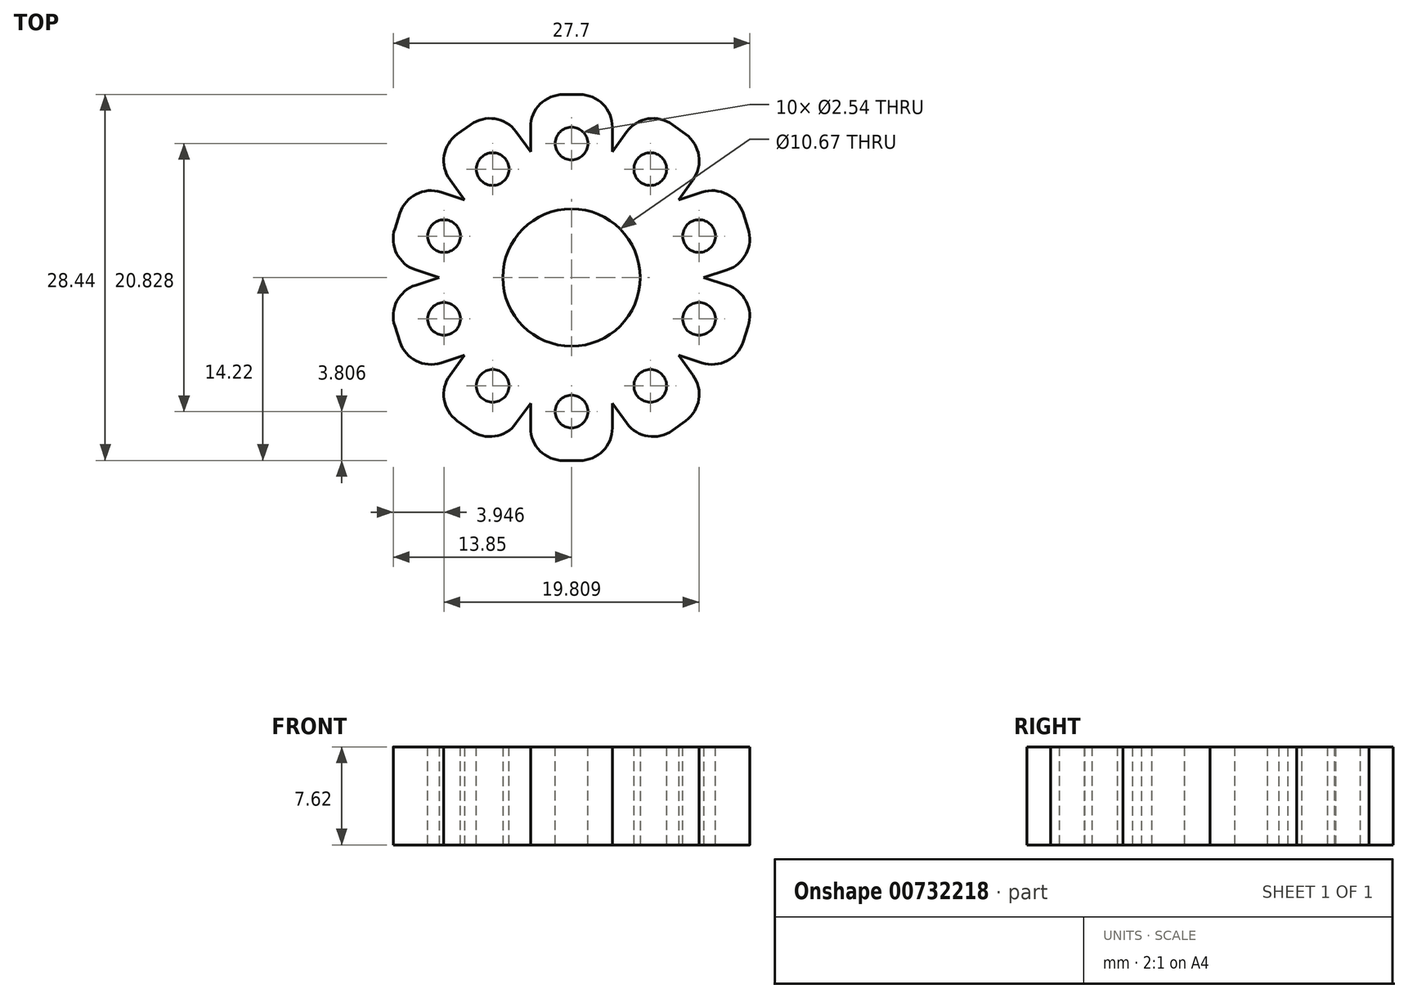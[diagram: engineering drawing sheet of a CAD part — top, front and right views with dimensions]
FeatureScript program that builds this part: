
annotation { "Feature Type Name" : "Feature", "Feature Type Description" : "" }
export const myFeature = defineFeature(function(context is Context, id is Id, definition is map)
    precondition{}
    {
        {
            var Q0;
            Q0=qCreatedBy(makeId("Top.planeOp"),FACE);
            var sketch = newSketch(context, id + "F0", { "sketchPlane" : qUnion([Q0])});
            skCircle(sketch, "E0", {"center": v(0, 0) * mm, "radius": 5.33 * mm});
            skCircle(sketch, "E1", {"center": v(0, 0) * mm, "radius": 7.62 * mm});
            skSolve(sketch);
        }
        {
            var Q0;
            Q0=makeQuery(id+"F0.imprint","IMPRINT",FACE,{"disambiguationData":[TD([[makeQuery(id+"F0.imprint","IMPRINT",EDGE,{"derivedFrom":sQuery(id+"F0.wireOp",EDGE,"E0")}),-1.0]])]});
            extrude(context, id + "F1", {"entities" : qUnion([Q0]), "depth" : 7.62 * mm, "offsetDistance" : 25.4 * mm});
        }
        {
            var Q0;
            Q0=makeQuery(id+"F1.opExtrude","CAP_FACE",FACE,{"disambiguationData":[OSD([sQuery(id+"F0.wireOp",EDGE,"E0"),sQuery(id+"F0.wireOp",EDGE,"E1")])],"isStart":false});
            var sketch = newSketch(context, id + "F2", { "sketchPlane" : qUnion([Q0])});
            skLineSegment(sketch, "E2", {"start": v(3.18, 5.33) * mm, "end": v(-3.18, 5.33) * mm});
            skLineSegment(sketch, "E3", {"start": v(-3.17, 5.33) * mm, "end": v(-3.18, 14.22) * mm});
            skLineSegment(sketch, "E4", {"start": v(-3.18, 14.22) * mm, "end": v(3.17, 14.22) * mm});
            skLineSegment(sketch, "E5", {"start": v(3.17, 14.22) * mm, "end": v(3.18, 5.33) * mm});
            skCircle(sketch, "E6", {"center": v(0, 10.41) * mm, "radius": 1.27 * mm});
            skSolve(sketch);
        }
        {
            var Q0;
            {var subQ1=sQuery(id+"F2.wireOp",EDGE,"E4");Q0=makeQuery(id+"F2.imprint","IMPRINT",FACE,{"disambiguationData":[TD([[makeQuery(id+"F2.imprint","IMPRINT",EDGE,{"derivedFrom":subQ1}),-1.0]])]});}
            extrude(context, id + "F3", {"entities" : qUnion([Q0]), "operationType" : NewBodyOperationType.ADD, "oppositeDirection" : true, "depth" : 7.62 * mm, "offsetDistance" : 25.4 * mm});
        }
        {
            var Q0;
            Q0=makeQuery(id+"F3.opExtrude","SWEPT_EDGE",EDGE,{"disambiguationData":[OSD([sQuery(id+"F2.wireOp",EDGE,"E4"),sQuery(id+"F2.wireOp",EDGE,"E5")])]});
            var Q1;
            Q1=makeQuery(id+"F3.opExtrude","SWEPT_EDGE",EDGE,{"disambiguationData":[OSD([sQuery(id+"F2.wireOp",EDGE,"E3"),sQuery(id+"F2.wireOp",EDGE,"E4")])]});
            fillet(context, id + "F4", {"entities" : qUnion([Q0, Q1]), "radius" : 2.54 * mm, "tangentPropagation" : true, "allowEdgeOverflow" : false});
        }
        {
            var Q0;
            Q0=makeQuery(id+"F1.opExtrude","SWEPT_BODY",BODY,{"disambiguationData":[OSD([sQuery(id+"F0.wireOp",EDGE,"E0"),sQuery(id+"F0.wireOp",EDGE,"E1")])]});
            var Q1;
            Q1=makeQuery(id+"F1.opExtrude","CAP_EDGE",EDGE,{"disambiguationData":[OSD([sQuery(id+"F0.wireOp",EDGE,"E0")])],"isStart":true});
            circularPattern(context, id + "F5", {"operationType" : NewBodyOperationType.ADD, "entities" : qUnion([Q0]), "axis" : qUnion([Q1]), "angle" : 360 * degree, "instanceCount" : 10, "equalSpace" : true});
        }
    });
